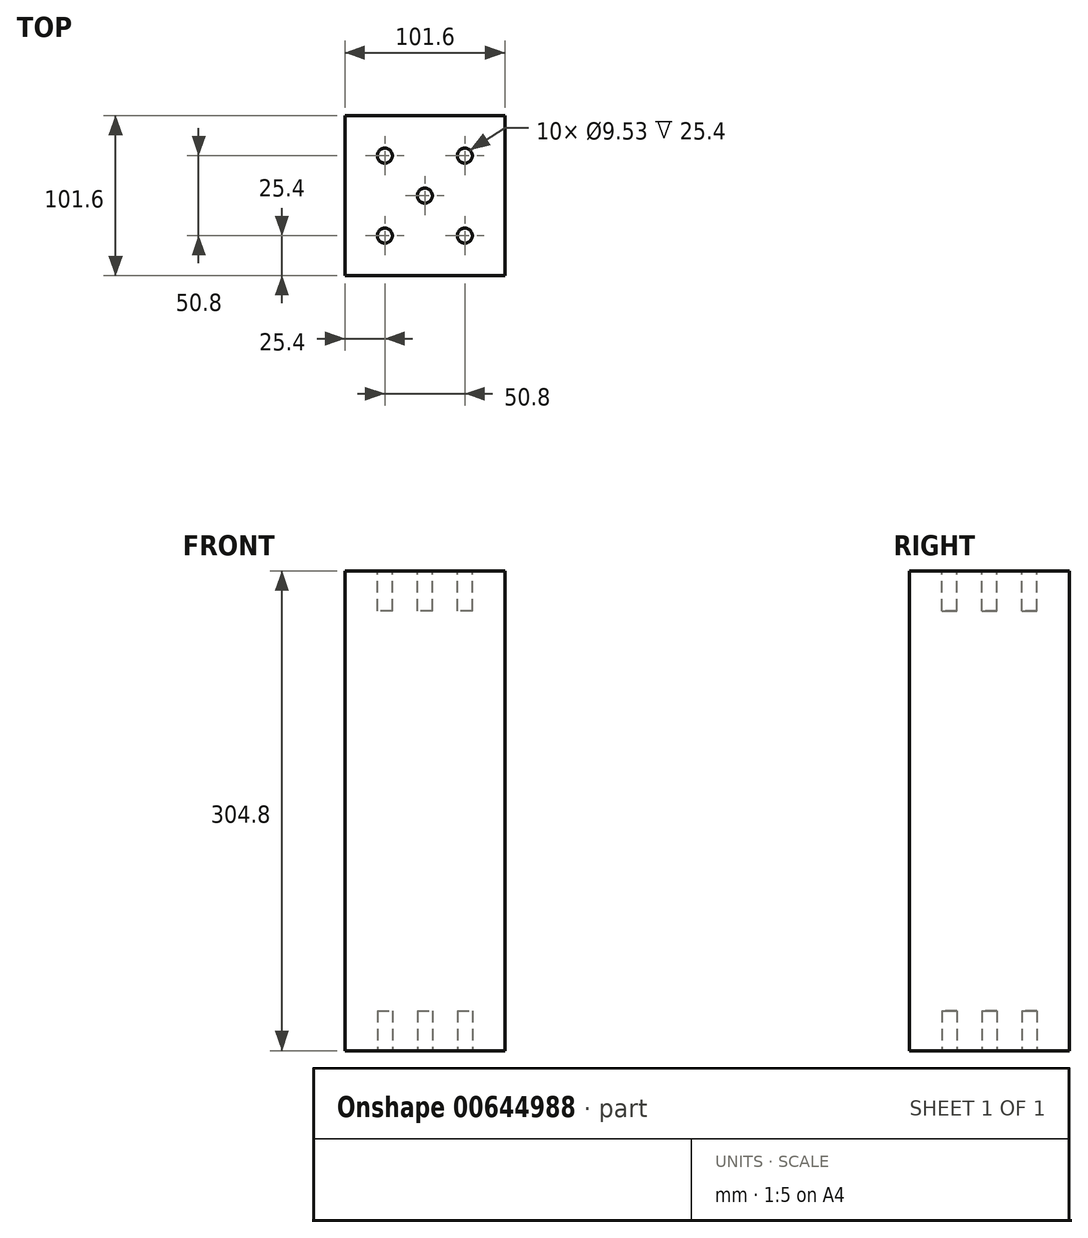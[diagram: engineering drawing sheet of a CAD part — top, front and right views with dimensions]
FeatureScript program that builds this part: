
annotation { "Feature Type Name" : "Feature", "Feature Type Description" : "" }
export const myFeature = defineFeature(function(context is Context, id is Id, definition is map)
    precondition{}
    {
        {
            var Q0;
            Q0=qCreatedBy(makeId("Top.planeOp"),FACE);
            var sketch = newSketch(context, id + "F0", { "sketchPlane" : qUnion([Q0])});
            skLineSegment(sketch, "E0.bottom", {"start": v(50.8, 50.8) * mm, "end": v(-50.8, 50.8) * mm});
            skLineSegment(sketch, "E0.top", {"start": v(50.8, -50.8) * mm, "end": v(-50.8, -50.8) * mm});
            skLineSegment(sketch, "E0.left", {"start": v(50.8, 50.8) * mm, "end": v(50.8, -50.8) * mm});
            skLineSegment(sketch, "E0.right", {"start": v(-50.8, 50.8) * mm, "end": v(-50.8, -50.8) * mm});
            skPoint(sketch, "E0.middle", {"position": v(0, 0) * mm});
            skSolve(sketch);
        }
        {
            var Q0;
            Q0=makeQuery(id+"F0.imprint","IMPRINT",FACE,{"disambiguationData":[TD([[makeQuery(id+"F0.imprint","IMPRINT",EDGE,{"derivedFrom":sQuery(id+"F0.wireOp",EDGE,"E0.bottom")}),1.0]])]});
            extrude(context, id + "F1", {"entities" : qUnion([Q0]), "depth" : 304.8 * mm, "offsetDistance" : 25.4 * mm});
        }
        {
            var Q0;
            Q0=makeQuery(id+"F1.opExtrude","CAP_FACE",FACE,{"disambiguationData":[OSD([sQuery(id+"F0.wireOp",EDGE,"E0.bottom"),sQuery(id+"F0.wireOp",EDGE,"E0.top"),sQuery(id+"F0.wireOp",EDGE,"E0.left"),sQuery(id+"F0.wireOp",EDGE,"E0.right")])],"isStart":false});
            var sketch = newSketch(context, id + "F2", { "sketchPlane" : qUnion([Q0])});
            skLineSegment(sketch, "E1.bottom", {"start": v(-50.8, -50.8) * mm, "end": v(0, -50.8) * mm});
            skLineSegment(sketch, "E1.top", {"start": v(-50.8, 0) * mm, "end": v(0, 0) * mm});
            skLineSegment(sketch, "E1.left", {"start": v(-50.8, -50.8) * mm, "end": v(-50.8, 0) * mm});
            skLineSegment(sketch, "E1.right", {"start": v(0, -50.8) * mm, "end": v(0, 0) * mm});
            skCircle(sketch, "E2", {"center": v(0, 0) * mm, "radius": 4.76 * mm});
            skCircle(sketch, "E3", {"center": v(-25.4, -25.4) * mm, "radius": 4.76 * mm});
            skPoint(sketch, "E3.centerSnap0", {"position": v(0, -25.4) * mm});
            skPoint(sketch, "E3.centerSnap1", {"position": v(-25.4, 0) * mm});
            skLineSegment(sketch, "E4.bottom", {"start": v(-50.8, 50.8) * mm, "end": v(0, 50.8) * mm});
            skLineSegment(sketch, "E4.left", {"start": v(-50.8, 50.8) * mm, "end": v(-50.8, 0) * mm});
            skLineSegment(sketch, "E4.right", {"start": v(0, 50.8) * mm, "end": v(0, 0) * mm});
            skLineSegment(sketch, "E5.bottom", {"start": v(50.8, 50.8) * mm, "end": v(0, 50.8) * mm});
            skLineSegment(sketch, "E5.top", {"start": v(50.8, 0) * mm, "end": v(0, 0) * mm});
            skLineSegment(sketch, "E5.left", {"start": v(50.8, 50.8) * mm, "end": v(50.8, 0) * mm});
            skLineSegment(sketch, "E6.bottom", {"start": v(50.8, -50.8) * mm, "end": v(0, -50.8) * mm});
            skLineSegment(sketch, "E6.left", {"start": v(50.8, -50.8) * mm, "end": v(50.8, 0) * mm});
            skCircle(sketch, "E7", {"center": v(-25.4, 25.4) * mm, "radius": 4.76 * mm});
            skPoint(sketch, "E7.centerSnap0", {"position": v(0, 25.4) * mm});
            skCircle(sketch, "E8", {"center": v(25.4, 25.4) * mm, "radius": 4.76 * mm});
            skPoint(sketch, "E8.centerSnap0", {"position": v(25.4, 0) * mm});
            skCircle(sketch, "E9", {"center": v(25.4, -25.4) * mm, "radius": 4.76 * mm});
            skSolve(sketch);
        }
        {
            var Q0;
            Q0=makeQuery(id+"F2.imprint","IMPRINT",FACE,{"disambiguationData":[TD([[makeQuery(id+"F2.imprint","IMPRINT",EDGE,{"derivedFrom":sQuery(id+"F2.wireOp",EDGE,"E7")}),1.0]])]});
            var Q1;
            Q1=makeQuery(id+"F2.imprint","IMPRINT",FACE,{"disambiguationData":[TD([[makeQuery(id+"F2.imprint","IMPRINT",EDGE,{"derivedFrom":sQuery(id+"F2.wireOp",EDGE,"E8")}),1.0]])]});
            var Q2;
            Q2=makeQuery(id+"F2.imprint","IMPRINT",FACE,{"disambiguationData":[TD([[makeQuery(id+"F2.imprint","IMPRINT",EDGE,{"derivedFrom":sQuery(id+"F2.wireOp",EDGE,"E9")}),1.0]])]});
            var Q3;
            {var subQ0=sQuery(id+"F2.wireOp",EDGE,"E5.top");var subQ1=sQuery(id+"F2.wireOp",EDGE,"E2");var subQ2=makeQuery(id+"F2.imprint","INTERSECT",VERTEX,{"derivedFrom":[subQ1,subQ0]});Q3=makeQuery(id+"F2.imprint","IMPRINT",FACE,{"disambiguationData":[TD([[makeQuery(id+"F2.imprint","IMPRINT",EDGE,{"disambiguationData":[TD([[subQ2,1.0]])],"derivedFrom":subQ1}),1.0]])]});}
            var Q4;
            {var subQ0=sQuery(id+"F2.wireOp",EDGE,"E4.right");var subQ1=sQuery(id+"F2.wireOp",EDGE,"E2");var subQ2=makeQuery(id+"F2.imprint","INTERSECT",VERTEX,{"derivedFrom":[subQ1,subQ0]});Q4=makeQuery(id+"F2.imprint","IMPRINT",FACE,{"disambiguationData":[TD([[makeQuery(id+"F2.imprint","IMPRINT",EDGE,{"disambiguationData":[TD([[subQ2,1.0]])],"derivedFrom":subQ1}),1.0]])]});}
            var Q5;
            {var subQ0=sQuery(id+"F2.wireOp",EDGE,"E4.right");var subQ1=sQuery(id+"F2.wireOp",EDGE,"E2");var subQ2=makeQuery(id+"F2.imprint","INTERSECT",VERTEX,{"derivedFrom":[subQ1,subQ0]});Q5=makeQuery(id+"F2.imprint","IMPRINT",FACE,{"disambiguationData":[TD([[makeQuery(id+"F2.imprint","IMPRINT",EDGE,{"disambiguationData":[TD([[subQ2,-1.0]])],"derivedFrom":subQ1}),1.0]])]});}
            var Q6;
            {var subQ0=sQuery(id+"F2.wireOp",EDGE,"E1.top");var subQ1=sQuery(id+"F2.wireOp",EDGE,"E2");var subQ2=makeQuery(id+"F2.imprint","INTERSECT",VERTEX,{"derivedFrom":[subQ1,subQ0]});Q6=makeQuery(id+"F2.imprint","IMPRINT",FACE,{"disambiguationData":[TD([[makeQuery(id+"F2.imprint","IMPRINT",EDGE,{"disambiguationData":[TD([[subQ2,-1.0]])],"derivedFrom":subQ1}),1.0]])]});}
            var Q7;
            Q7=makeQuery(id+"F2.imprint","IMPRINT",FACE,{"disambiguationData":[TD([[makeQuery(id+"F2.imprint","IMPRINT",EDGE,{"derivedFrom":sQuery(id+"F2.wireOp",EDGE,"E3")}),1.0]])]});
            extrude(context, id + "F3", {"entities" : qUnion([Q0, Q1, Q2, Q3, Q4, Q5, Q6, Q7]), "operationType" : NewBodyOperationType.REMOVE, "oppositeDirection" : true, "depth" : 25.4 * mm, "offsetDistance" : 25.4 * mm});
        }
        {
            var Q0;
            Q0=makeQuery(id+"F1.opExtrude","CAP_FACE",FACE,{"disambiguationData":[OSD([sQuery(id+"F0.wireOp",EDGE,"E0.bottom"),sQuery(id+"F0.wireOp",EDGE,"E0.top"),sQuery(id+"F0.wireOp",EDGE,"E0.left"),sQuery(id+"F0.wireOp",EDGE,"E0.right")])],"isStart":true});
            var sketch = newSketch(context, id + "F4", { "sketchPlane" : qUnion([Q0])});
            skLineSegment(sketch, "E10.bottom", {"start": v(-50.8, 50.8) * mm, "end": v(0, 50.8) * mm});
            skLineSegment(sketch, "E10.top", {"start": v(-50.8, 0) * mm, "end": v(0, 0) * mm});
            skLineSegment(sketch, "E10.left", {"start": v(-50.8, 50.8) * mm, "end": v(-50.8, 0) * mm});
            skLineSegment(sketch, "E10.right", {"start": v(0, 50.8) * mm, "end": v(0, 0) * mm});
            skLineSegment(sketch, "E11.bottom", {"start": v(50.8, 50.8) * mm, "end": v(0, 50.8) * mm});
            skLineSegment(sketch, "E11.top", {"start": v(50.8, 0) * mm, "end": v(0, 0) * mm});
            skLineSegment(sketch, "E11.left", {"start": v(50.8, 50.8) * mm, "end": v(50.8, 0) * mm});
            skLineSegment(sketch, "E12.bottom", {"start": v(50.8, -50.8) * mm, "end": v(0, -50.8) * mm});
            skLineSegment(sketch, "E12.left", {"start": v(50.8, -50.8) * mm, "end": v(50.8, 0) * mm});
            skLineSegment(sketch, "E12.right", {"start": v(0, -50.8) * mm, "end": v(0, 0) * mm});
            skLineSegment(sketch, "E13.bottom", {"start": v(-50.8, -50.8) * mm, "end": v(0, -50.8) * mm});
            skLineSegment(sketch, "E13.left", {"start": v(-50.8, -50.8) * mm, "end": v(-50.8, 0) * mm});
            skCircle(sketch, "E14", {"center": v(0, 0) * mm, "radius": 4.76 * mm});
            skCircle(sketch, "E15", {"center": v(-25.4, -25.4) * mm, "radius": 4.76 * mm});
            skPoint(sketch, "E15.centerSnap0", {"position": v(0, -25.4) * mm});
            skPoint(sketch, "E15.centerSnap1", {"position": v(-25.4, 0) * mm});
            skCircle(sketch, "E16", {"center": v(25.4, -25.4) * mm, "radius": 4.76 * mm});
            skPoint(sketch, "E16.centerSnap0", {"position": v(25.4, 0) * mm});
            skCircle(sketch, "E17", {"center": v(25.4, 25.4) * mm, "radius": 4.76 * mm});
            skPoint(sketch, "E17.centerSnap0", {"position": v(0, 25.4) * mm});
            skCircle(sketch, "E18", {"center": v(-25.4, 25.4) * mm, "radius": 4.76 * mm});
            skSolve(sketch);
        }
        {
            var Q0;
            Q0=makeQuery(id+"F4.imprint","IMPRINT",FACE,{"disambiguationData":[TD([[makeQuery(id+"F4.imprint","IMPRINT",EDGE,{"derivedFrom":sQuery(id+"F4.wireOp",EDGE,"E18")}),1.0]])]});
            var Q1;
            Q1=makeQuery(id+"F4.imprint","IMPRINT",FACE,{"disambiguationData":[TD([[makeQuery(id+"F4.imprint","IMPRINT",EDGE,{"derivedFrom":sQuery(id+"F4.wireOp",EDGE,"E17")}),1.0]])]});
            var Q2;
            Q2=makeQuery(id+"F4.imprint","IMPRINT",FACE,{"disambiguationData":[TD([[makeQuery(id+"F4.imprint","IMPRINT",EDGE,{"derivedFrom":sQuery(id+"F4.wireOp",EDGE,"E16")}),1.0]])]});
            var Q3;
            Q3=makeQuery(id+"F4.imprint","IMPRINT",FACE,{"disambiguationData":[TD([[makeQuery(id+"F4.imprint","IMPRINT",EDGE,{"derivedFrom":sQuery(id+"F4.wireOp",EDGE,"E15")}),1.0]])]});
            var Q4;
            {var subQ1=sQuery(id+"F4.wireOp",EDGE,"E10.top");var subQ3=sQuery(id+"F4.wireOp",EDGE,"E14");var subQ4=makeQuery(id+"F4.imprint","INTERSECT",VERTEX,{"derivedFrom":[subQ1,subQ3]});Q4=makeQuery(id+"F4.imprint","IMPRINT",FACE,{"disambiguationData":[TD([[makeQuery(id+"F4.imprint","IMPRINT",EDGE,{"disambiguationData":[TD([[subQ4,-1.0]])],"derivedFrom":subQ3}),1.0]])]});}
            var Q5;
            {var subQ1=sQuery(id+"F4.wireOp",EDGE,"E10.right");var subQ3=sQuery(id+"F4.wireOp",EDGE,"E14");var subQ4=makeQuery(id+"F4.imprint","INTERSECT",VERTEX,{"derivedFrom":[subQ1,subQ3]});Q5=makeQuery(id+"F4.imprint","IMPRINT",FACE,{"disambiguationData":[TD([[makeQuery(id+"F4.imprint","IMPRINT",EDGE,{"disambiguationData":[TD([[subQ4,-1.0]])],"derivedFrom":subQ3}),1.0]])]});}
            var Q6;
            {var subQ1=sQuery(id+"F4.wireOp",EDGE,"E10.right");var subQ3=sQuery(id+"F4.wireOp",EDGE,"E14");var subQ4=makeQuery(id+"F4.imprint","INTERSECT",VERTEX,{"derivedFrom":[subQ1,subQ3]});Q6=makeQuery(id+"F4.imprint","IMPRINT",FACE,{"disambiguationData":[TD([[makeQuery(id+"F4.imprint","IMPRINT",EDGE,{"disambiguationData":[TD([[subQ4,1.0]])],"derivedFrom":subQ3}),1.0]])]});}
            var Q7;
            {var subQ1=sQuery(id+"F4.wireOp",EDGE,"E11.top");var subQ3=sQuery(id+"F4.wireOp",EDGE,"E14");var subQ4=makeQuery(id+"F4.imprint","INTERSECT",VERTEX,{"derivedFrom":[subQ1,subQ3]});Q7=makeQuery(id+"F4.imprint","IMPRINT",FACE,{"disambiguationData":[TD([[makeQuery(id+"F4.imprint","IMPRINT",EDGE,{"disambiguationData":[TD([[subQ4,1.0]])],"derivedFrom":subQ3}),1.0]])]});}
            extrude(context, id + "F5", {"entities" : qUnion([Q0, Q1, Q2, Q3, Q4, Q5, Q6, Q7]), "operationType" : NewBodyOperationType.REMOVE, "oppositeDirection" : true, "depth" : 25.4 * mm, "offsetDistance" : 25.4 * mm});
        }
    });
